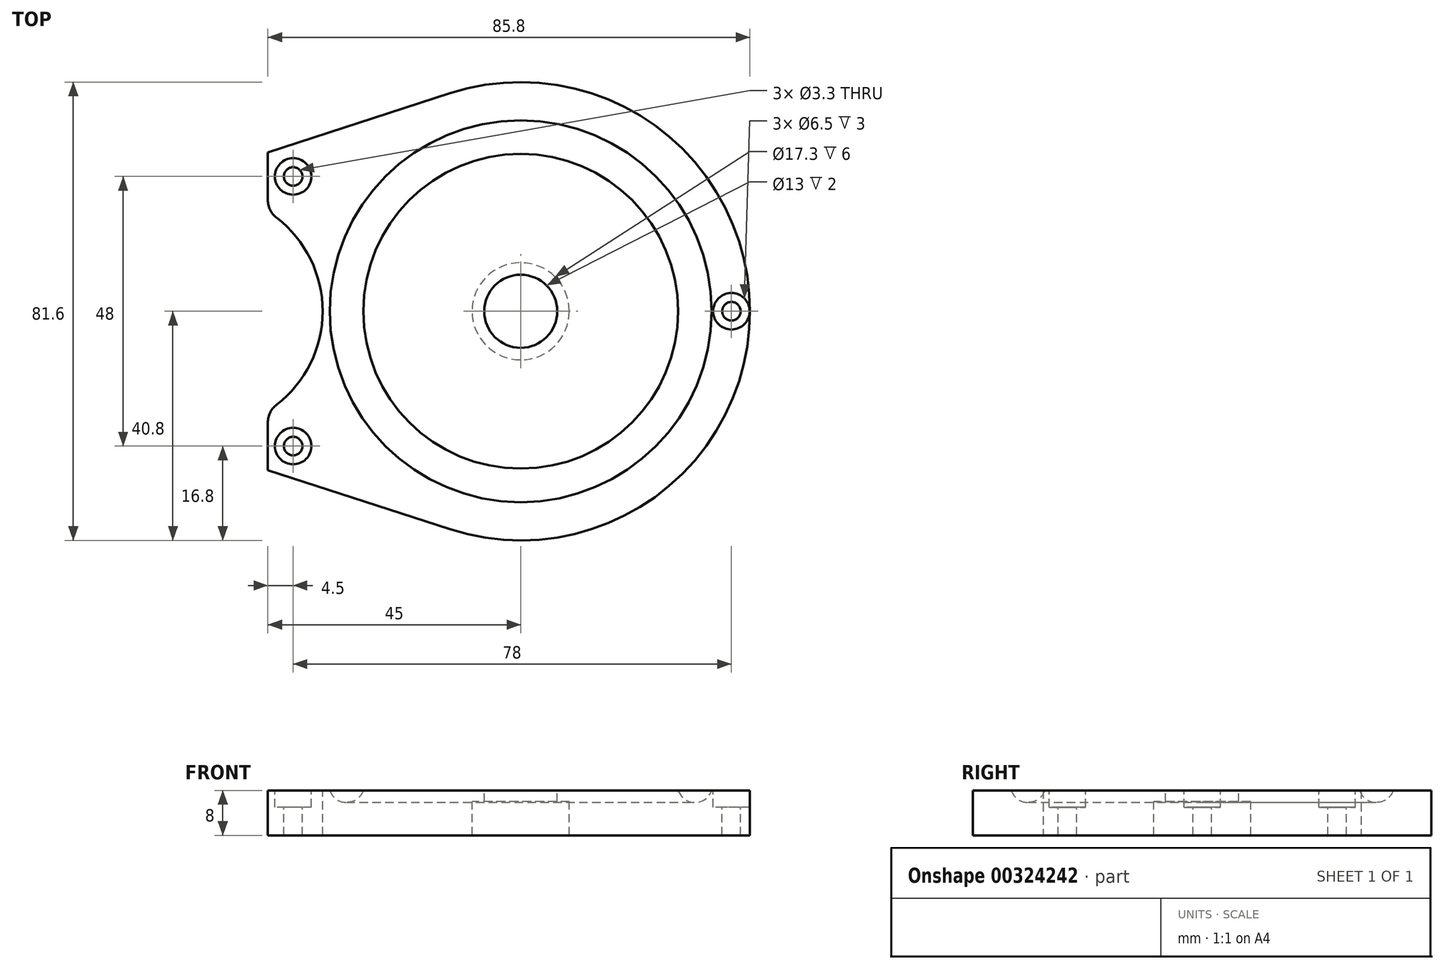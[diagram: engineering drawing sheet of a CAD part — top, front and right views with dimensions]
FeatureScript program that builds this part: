
annotation { "Feature Type Name" : "Feature", "Feature Type Description" : "" }
export const myFeature = defineFeature(function(context is Context, id is Id, definition is map)
    precondition{}
    {
        {
            var Q0;
            Q0=qCreatedBy(makeId("Top.planeOp"),FACE);
            var sketch = newSketch(context, id + "F0", { "sketchPlane" : qUnion([Q0])});
            skCircle(sketch, "E0", {"center": v(0, 0) * mm, "radius": 40.8 * mm});
            skSolve(sketch);
        }
        {
            var Q0;
            Q0=qSketchRegion(id+"F0",true);
            extrude(context, id + "F1", {"entities" : qUnion([Q0]), "depth" : 8 * mm});
        }
        {
            var Q0;
            Q0=qCreatedBy(makeId("Right.planeOp"),FACE);
            var sketch = newSketch(context, id + "F2", { "sketchPlane" : qUnion([Q0])});
            skLineSegment(sketch, "E1", {"start": v(0, 0) * mm, "end": v(0, 8) * mm});
            skLineSegment(sketch, "E2", {"start": v(0, 8) * mm, "end": v(6.5, 8) * mm});
            skLineSegment(sketch, "E3", {"start": v(6.5, 8) * mm, "end": v(6.5, 6) * mm});
            skLineSegment(sketch, "E4", {"start": v(6.5, 6) * mm, "end": v(8.65, 6) * mm});
            skLineSegment(sketch, "E5", {"start": v(8.65, 6) * mm, "end": v(8.65, 0) * mm});
            skLineSegment(sketch, "E6", {"start": v(8.65, 0) * mm, "end": v(0, 0) * mm});
            skLineSegment(sketch, "E7", {"start": v(0, 8) * mm, "end": v(0, 13.47) * mm, "construction": true});
            skSolve(sketch);
        }
        {
            var Q0;
            Q0=qSketchRegion(id+"F2",true);
            var Q1;
            Q1=sQuery(id+"F2.wireOp",EDGE,"E7");
            revolve(context, id + "F3", {"operationType" : NewBodyOperationType.REMOVE, "entities" : qUnion([Q0]), "axis" : qUnion([Q1]), "revolveType" : RevolveType.FULL, "oppositeDirection" : true});
        }
        {
            var Q0;
            Q0=qCreatedBy(makeId("Right.planeOp"),FACE);
            var sketch = newSketch(context, id + "F4", { "sketchPlane" : qUnion([Q0])});
            skCircle(sketch, "E8", {"center": v(31, 9) * mm, "radius": 3.15 * mm});
            skLineSegment(sketch, "E9", {"start": v(0, -0.8) * mm, "end": v(0, 13.57) * mm, "construction": true});
            skSolve(sketch);
        }
        {
            var Q0;
            Q0=qSketchRegion(id+"F4",true);
            var Q1;
            Q1=sQuery(id+"F4.wireOp",EDGE,"E9");
            revolve(context, id + "F5", {"operationType" : NewBodyOperationType.REMOVE, "entities" : qUnion([Q0]), "axis" : qUnion([Q1]), "revolveType" : RevolveType.FULL, "oppositeDirection" : true});
        }
        {
            var Q0;
            Q0=qCreatedBy(makeId("Top.planeOp"),FACE);
            var sketch = newSketch(context, id + "F6", { "sketchPlane" : qUnion([Q0])});
            skLineSegment(sketch, "E10.bottom", {"start": v(-36, 19.2) * mm, "end": v(-40.8, 19.2) * mm});
            skLineSegment(sketch, "E10.top", {"start": v(-36, -19.2) * mm, "end": v(-40.8, -19.2) * mm});
            skLineSegment(sketch, "E10.left", {"start": v(-36, 19.2) * mm, "end": v(-36, -19.2) * mm});
            skLineSegment(sketch, "E10.right", {"start": v(-40.8, 19.2) * mm, "end": v(-40.8, -19.2) * mm});
            skSolve(sketch);
        }
        {
            var Q0;
            Q0=qSketchRegion(id+"F6",true);
            extrude(context, id + "F7", {"entities" : qUnion([Q0]), "operationType" : NewBodyOperationType.REMOVE, "endBound" : BoundingType.THROUGH_ALL, "depth" : 25 * mm});
        }
        {
            var Q0;
            Q0=qCreatedBy(makeId("Top.planeOp"),FACE);
            var sketch = newSketch(context, id + "F8", { "sketchPlane" : qUnion([Q0])});
            skLineSegment(sketch, "E11", {"start": v(-45, -28.28) * mm, "end": v(-45, 28.28) * mm});
            skLineSegment(sketch, "E12", {"start": v(-45, 28.28) * mm, "end": v(-12.6, 38.8) * mm});
            skLineSegment(sketch, "E13", {"start": v(0, 0) * mm, "end": v(-51.86, 0) * mm, "construction": true});
            skArc(sketch, "E14.0", {"start": v(-12.6, 38.8) * mm, "mid": v(-26.2, 31.27) * mm, "end": v(-36, 19.2) * mm});
            skPoint(sketch, "E15.orphan", {"position": v(-36, -19.2) * mm});
            skLineSegment(sketch, "E16.MirrorCS", {"start": v(-45, -28.28) * mm, "end": v(-12.6, -38.8) * mm});
            skArc(sketch, "E17.MirrorCS", {"start": v(-12.6, -38.8) * mm, "mid": v(-26.2, -31.27) * mm, "end": v(-36, -19.2) * mm});
            skLineSegment(sketch, "E18", {"start": v(-36, 19.2) * mm, "end": v(-36, -19.2) * mm});
            skSolve(sketch);
        }
        {
            var Q0;
            Q0=qSketchRegion(id+"F8",true);
            var Q1;
            {var subQ0=sQuery(id+"F0.wireOp",EDGE,"E0");Q1=makeQuery(id+"F5.boolean.opBoolean","SPLIT",FACE,{"disambiguationData":[TD([makeQuery(id+"F1.opExtrude","SWEPT_FACE",FACE,{"disambiguationData":[OSD([subQ0])]})])],"derivedFrom":makeQuery(id+"F1.opExtrude","CAP_FACE",FACE,{"disambiguationData":[OSD([subQ0])],"isStart":false})});}
            extrude(context, id + "F9", {"entities" : qUnion([Q0]), "operationType" : NewBodyOperationType.ADD, "endBound" : BoundingType.UP_TO_SURFACE, "endBoundEntityFace" : qUnion([Q1]), "depth" : 25 * mm});
        }
        {
            var Q0;
            {var subQ0=sQuery(id+"F0.wireOp",EDGE,"E0");Q0=makeQuery(id+"F9.boolean.opBoolean","MERGE",FACE,{"derivedFrom":[makeQuery(id+"F5.boolean.opBoolean","SPLIT",FACE,{"disambiguationData":[TD([makeQuery(id+"F1.opExtrude","SWEPT_FACE",FACE,{"disambiguationData":[OSD([subQ0])]})])],"derivedFrom":makeQuery(id+"F1.opExtrude","CAP_FACE",FACE,{"disambiguationData":[OSD([subQ0])],"isStart":false})}),makeQuery(id+"F9.opExtrude","CAP_FACE",FACE,{"disambiguationData":[OSD([sQuery(id+"F8.wireOp",EDGE,"E11"),sQuery(id+"F8.wireOp",EDGE,"E12"),sQuery(id+"F8.wireOp",EDGE,"E14.0"),sQuery(id+"F8.wireOp",EDGE,"E16.MirrorCS"),sQuery(id+"F8.wireOp",EDGE,"E17.MirrorCS"),sQuery(id+"F8.wireOp",EDGE,"E18")])],"isStart":false})]});}
            var sketch = newSketch(context, id + "F10", { "sketchPlane" : qUnion([Q0])});
            skCircle(sketch, "E19", {"center": v(-56.25, 0) * mm, "radius": 21 * mm});
            skLineSegment(sketch, "E20", {"start": v(-56.25, 0) * mm, "end": v(0, 0) * mm, "construction": true});
            skSolve(sketch);
        }
        {
            var Q0;
            Q0=qSketchRegion(id+"F10",true);
            extrude(context, id + "F11", {"entities" : qUnion([Q0]), "operationType" : NewBodyOperationType.REMOVE, "endBound" : BoundingType.THROUGH_ALL, "oppositeDirection" : true, "depth" : 25 * mm});
        }
        {
            var Q0;
            Q0=makeQuery(id+"F11.boolean.opBoolean","INTERSECT",EDGE,{"disambiguationData":[OD(1.0)],"derivedFrom":[makeQuery(id+"F9.opExtrude","SWEPT_FACE",FACE,{"disambiguationData":[OSD([sQuery(id+"F8.wireOp",EDGE,"E11")])]}),makeQuery(id+"F11.opExtrude","SWEPT_FACE",FACE,{"disambiguationData":[OSD([sQuery(id+"F10.wireOp",EDGE,"E19")])]})]});
            var Q1;
            Q1=makeQuery(id+"F11.boolean.opBoolean","INTERSECT",EDGE,{"disambiguationData":[OD(0.0)],"derivedFrom":[makeQuery(id+"F9.opExtrude","SWEPT_FACE",FACE,{"disambiguationData":[OSD([sQuery(id+"F8.wireOp",EDGE,"E11")])]}),makeQuery(id+"F11.opExtrude","SWEPT_FACE",FACE,{"disambiguationData":[OSD([sQuery(id+"F10.wireOp",EDGE,"E19")])]})]});
            fillet(context, id + "F12", {"entities" : qUnion([Q0, Q1]), "radius" : 4 * mm, "tangentPropagation" : true, "allowEdgeOverflow" : false});
        }
        {
            var Q0;
            {var subQ0=sQuery(id+"F0.wireOp",EDGE,"E0");Q0=makeQuery(id+"F9.boolean.opBoolean","MERGE",FACE,{"derivedFrom":[makeQuery(id+"F5.boolean.opBoolean","SPLIT",FACE,{"disambiguationData":[TD([makeQuery(id+"F1.opExtrude","SWEPT_FACE",FACE,{"disambiguationData":[OSD([subQ0])]})])],"derivedFrom":makeQuery(id+"F1.opExtrude","CAP_FACE",FACE,{"disambiguationData":[OSD([subQ0])],"isStart":false})}),makeQuery(id+"F9.opExtrude","CAP_FACE",FACE,{"disambiguationData":[OSD([sQuery(id+"F8.wireOp",EDGE,"E11"),sQuery(id+"F8.wireOp",EDGE,"E12"),sQuery(id+"F8.wireOp",EDGE,"E14.0"),sQuery(id+"F8.wireOp",EDGE,"E16.MirrorCS"),sQuery(id+"F8.wireOp",EDGE,"E17.MirrorCS"),sQuery(id+"F8.wireOp",EDGE,"E18")])],"isStart":false})]});}
            var sketch = newSketch(context, id + "F13", { "sketchPlane" : qUnion([Q0])});
            skPoint(sketch, "E21", {"position": v(-40.5, 24) * mm});
            skPoint(sketch, "E22", {"position": v(37.5, 0) * mm});
            skLineSegment(sketch, "E23", {"start": v(0, 0) * mm, "end": v(47.97, 0) * mm, "construction": true});
            skPoint(sketch, "E24.MirrorP", {"position": v(-40.5, -24) * mm});
            skSolve(sketch);
        }
        {
            var Q0;
            Q0=sQuery(id+"F13.wireOp",VERTEX,"E21");
            var Q1;
            Q1=sQuery(id+"F13.wireOp",VERTEX,"E24.MirrorP");
            var Q2;
            Q2=sQuery(id+"F13.wireOp",VERTEX,"E22");
            var Q3;
            Q3=makeQuery(id+"F1.opExtrude","SWEPT_BODY",BODY,{"disambiguationData":[OSD([sQuery(id+"F0.wireOp",EDGE,"E0")])]});
            hole(context, id + "F14", {"style" : HoleStyle.C_BORE, "endStyle" : HoleEndStyle.THROUGH, "standardTappedOrClearance" : lookupTablePath({ "standard" : "ISO", "fit" : "Normal", "size" : "M3", "type" : "Clearance" }), "standardBlindInLast" : lookupTablePath({ "fit" : "Standard", "standard" : "ISO", "size" : "M3", "type" : "Clearance" }), "holeDiameter" : 3.3 * mm, "cBoreDiameter" : 6.5 * mm, "cBoreDepth" : 3 * mm, "tappedDepth" : 12 * mm, "tapClearance" : 3, "locations" : qUnion([Q0, Q1, Q2]), "scope" : qUnion([Q3])});
        }
    });
